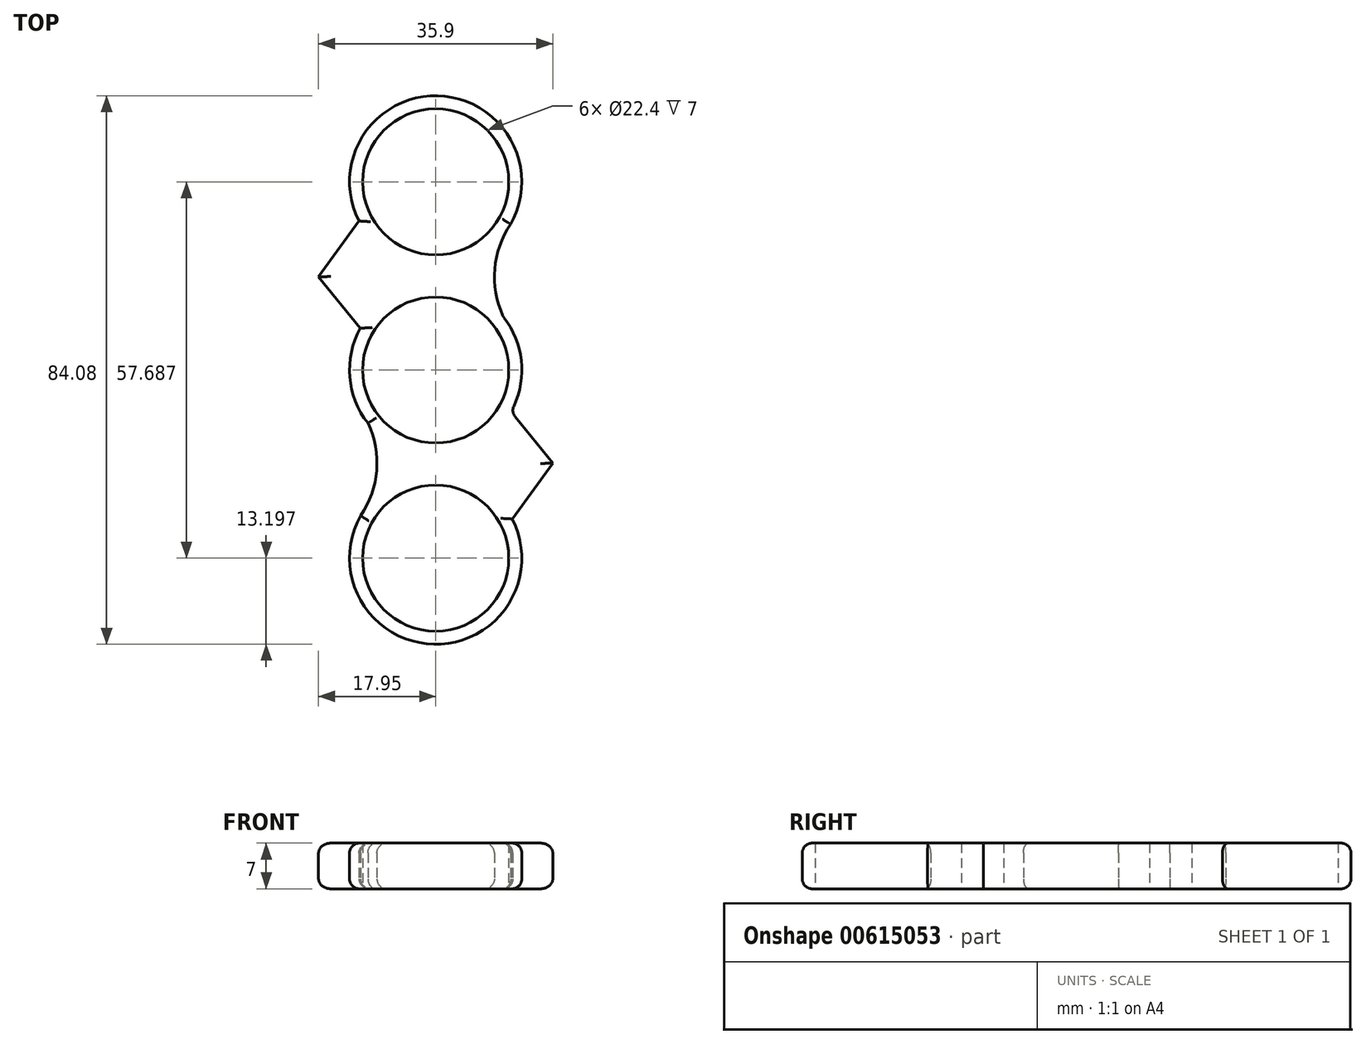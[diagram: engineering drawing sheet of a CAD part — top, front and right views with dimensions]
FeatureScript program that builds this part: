
annotation { "Feature Type Name" : "Feature", "Feature Type Description" : "" }
export const myFeature = defineFeature(function(context is Context, id is Id, definition is map)
    precondition{}
    {
        {
            var Q0;
            Q0=qCreatedBy(makeId("Top.planeOp"),FACE);
            var sketch = newSketch(context, id + "F0", { "sketchPlane" : qUnion([Q0])});
            skCircle(sketch, "E0", {"center": v(0, 0) * mm, "radius": 11.2 * mm});
            skArc(sketch, "E1", {"start": v(-11.55, 6.39) * mm, "mid": v(-13.16, -1.06) * mm, "end": v(-10.38, -8.16) * mm});
            skCircle(sketch, "E2", {"center": v(0, 28.84) * mm, "radius": 11.2 * mm});
            skArc(sketch, "E3", {"start": v(10.87, 21.35) * mm, "mid": v(0.87, 42.01) * mm, "end": v(-11.76, 22.85) * mm});
            skArc(sketch, "E4.1.0", {"start": v(-10.87, -21.35) * mm, "mid": v(-0.87, -42.01) * mm, "end": v(11.76, -22.85) * mm});
            skCircle(sketch, "E4.1.1", {"center": v(0, -28.84) * mm, "radius": 11.2 * mm});
            skArc(sketch, "E5", {"start": v(11.5, 22.35) * mm, "mid": v(9.04, 15.4) * mm, "end": v(10.38, 8.16) * mm});
            skArc(sketch, "E6.1.0", {"start": v(-11.5, -22.35) * mm, "mid": v(-9.04, -15.4) * mm, "end": v(-10.38, -8.16) * mm});
            skLineSegment(sketch, "E7", {"start": v(12.73, -25.34) * mm, "end": v(10.8, -25.88) * mm, "construction": true});
            skLineSegment(sketch, "E8", {"start": v(-12.6, 24.91) * mm, "end": v(-10.68, 25.47) * mm, "construction": true});
            skLineSegment(sketch, "E9", {"start": v(-8.29, 10.27) * mm, "end": v(-7.03, 8.72) * mm, "construction": true});
            skLineSegment(sketch, "E10", {"start": v(10.8, -2.96) * mm, "end": v(12.73, -3.5) * mm, "construction": true});
            skLineSegment(sketch, "E11", {"start": v(-10.76, 3.11) * mm, "end": v(-12.68, 3.67) * mm, "construction": true});
            skLineSegment(sketch, "E12", {"start": v(17.95, -14.29) * mm, "end": v(11.76, -22.85) * mm});
            skLineSegment(sketch, "E13", {"start": v(17.95, -14.29) * mm, "end": v(11.55, -6.39) * mm});
            skLineSegment(sketch, "E14.1.0", {"start": v(-17.95, 14.29) * mm, "end": v(-11.55, 6.39) * mm});
            skLineSegment(sketch, "E14.1.1", {"start": v(-17.95, 14.29) * mm, "end": v(-11.76, 22.85) * mm});
            skPoint(sketch, "E15.orphan", {"position": v(-23.26, 28.84) * mm});
            skLineSegment(sketch, "E16.trimOffspring", {"start": v(10.83, 31.68) * mm, "end": v(12.76, 32.24) * mm, "construction": true});
            skPoint(sketch, "E17.start.orphan", {"position": v(23.26, 35.27) * mm});
            skLineSegment(sketch, "E18.trimOffspring", {"start": v(-10.76, -31.94) * mm, "end": v(-12.69, -32.48) * mm, "construction": true});
            skPoint(sketch, "E19.orphan", {"position": v(-23.26, -35.45) * mm});
            skArc(sketch, "E20.trimOffspring", {"start": v(11.55, -6.39) * mm, "mid": v(13.16, 1.06) * mm, "end": v(10.38, 8.16) * mm});
            skSolve(sketch);
        }
        {
            var Q0;
            Q0=makeQuery(id+"F0.imprint","IMPRINT",FACE,{"disambiguationData":[TD([[makeQuery(id+"F0.imprint","IMPRINT",EDGE,{"derivedFrom":sQuery(id+"F0.wireOp",EDGE,"E0")}),-1.0]])]});
            extrude(context, id + "F1", {"entities" : qUnion([Q0]), "depth" : 7 * mm, "offsetDistance" : 25 * mm});
        }
        {
            var Q0;
            Q0=makeQuery(id+"F1.opExtrude","CAP_EDGE",EDGE,{"disambiguationData":[OSD([sQuery(id+"F0.wireOp",EDGE,"E5")])],"isStart":false});
            var Q1;
            Q1=makeQuery(id+"F1.opExtrude","CAP_EDGE",EDGE,{"disambiguationData":[OSD([sQuery(id+"F0.wireOp",EDGE,"E20.trimOffspring")])],"isStart":false});
            var Q2;
            Q2=makeQuery(id+"F1.opExtrude","CAP_EDGE",EDGE,{"disambiguationData":[OSD([sQuery(id+"F0.wireOp",EDGE,"E3")])],"isStart":false});
            var Q3;
            Q3=makeQuery(id+"F1.opExtrude","CAP_EDGE",EDGE,{"disambiguationData":[OSD([sQuery(id+"F0.wireOp",EDGE,"E14.1.1")])],"isStart":false});
            var Q4;
            Q4=makeQuery(id+"F1.opExtrude","CAP_EDGE",EDGE,{"disambiguationData":[OSD([sQuery(id+"F0.wireOp",EDGE,"E14.1.0")])],"isStart":false});
            var Q5;
            Q5=makeQuery(id+"F1.opExtrude","CAP_EDGE",EDGE,{"disambiguationData":[OSD([sQuery(id+"F0.wireOp",EDGE,"E1")])],"isStart":false});
            var Q6;
            Q6=makeQuery(id+"F1.opExtrude","CAP_EDGE",EDGE,{"disambiguationData":[OSD([sQuery(id+"F0.wireOp",EDGE,"E6.1.0")])],"isStart":false});
            var Q7;
            Q7=makeQuery(id+"F1.opExtrude","CAP_EDGE",EDGE,{"disambiguationData":[OSD([sQuery(id+"F0.wireOp",EDGE,"E4.1.0")])],"isStart":false});
            var Q8;
            Q8=makeQuery(id+"F1.opExtrude","CAP_EDGE",EDGE,{"disambiguationData":[OSD([sQuery(id+"F0.wireOp",EDGE,"E12")])],"isStart":false});
            var Q9;
            Q9=makeQuery(id+"F1.opExtrude","CAP_EDGE",EDGE,{"disambiguationData":[OSD([sQuery(id+"F0.wireOp",EDGE,"E13")])],"isStart":false});
            var Q10;
            Q10=makeQuery(id+"F1.opExtrude","CAP_EDGE",EDGE,{"disambiguationData":[OSD([sQuery(id+"F0.wireOp",EDGE,"E3")])],"isStart":true});
            var Q11;
            Q11=makeQuery(id+"F1.opExtrude","CAP_EDGE",EDGE,{"disambiguationData":[OSD([sQuery(id+"F0.wireOp",EDGE,"E5")])],"isStart":true});
            var Q12;
            Q12=makeQuery(id+"F1.opExtrude","SWEPT_FACE",FACE,{"disambiguationData":[OSD([sQuery(id+"F0.wireOp",EDGE,"E20.trimOffspring")])]});
            var Q13;
            Q13=makeQuery(id+"F1.opExtrude","CAP_EDGE",EDGE,{"disambiguationData":[OSD([sQuery(id+"F0.wireOp",EDGE,"E13")])],"isStart":true});
            var Q14;
            Q14=makeQuery(id+"F1.opExtrude","CAP_EDGE",EDGE,{"disambiguationData":[OSD([sQuery(id+"F0.wireOp",EDGE,"E4.1.0")])],"isStart":true});
            var Q15;
            Q15=makeQuery(id+"F1.opExtrude","CAP_EDGE",EDGE,{"disambiguationData":[OSD([sQuery(id+"F0.wireOp",EDGE,"E6.1.0")])],"isStart":true});
            var Q16;
            Q16=makeQuery(id+"F1.opExtrude","CAP_EDGE",EDGE,{"disambiguationData":[OSD([sQuery(id+"F0.wireOp",EDGE,"E1")])],"isStart":true});
            var Q17;
            Q17=makeQuery(id+"F1.opExtrude","CAP_EDGE",EDGE,{"disambiguationData":[OSD([sQuery(id+"F0.wireOp",EDGE,"E14.1.0")])],"isStart":true});
            var Q18;
            Q18=makeQuery(id+"F1.opExtrude","CAP_EDGE",EDGE,{"disambiguationData":[OSD([sQuery(id+"F0.wireOp",EDGE,"E14.1.1")])],"isStart":true});
            var Q19;
            Q19=makeQuery(id+"F1.opExtrude","CAP_EDGE",EDGE,{"disambiguationData":[OSD([sQuery(id+"F0.wireOp",EDGE,"E12")])],"isStart":true});
            fillet(context, id + "F2", {"entities" : qUnion([Q0, Q1, Q2, Q3, Q4, Q5, Q6, Q7, Q8, Q9, Q10, Q11, Q12, Q13, Q14, Q15, Q16, Q17, Q18, Q19]), "radius" : 1.5 * mm, "tangentPropagation" : true, "allowEdgeOverflow" : false});
        }
    });
